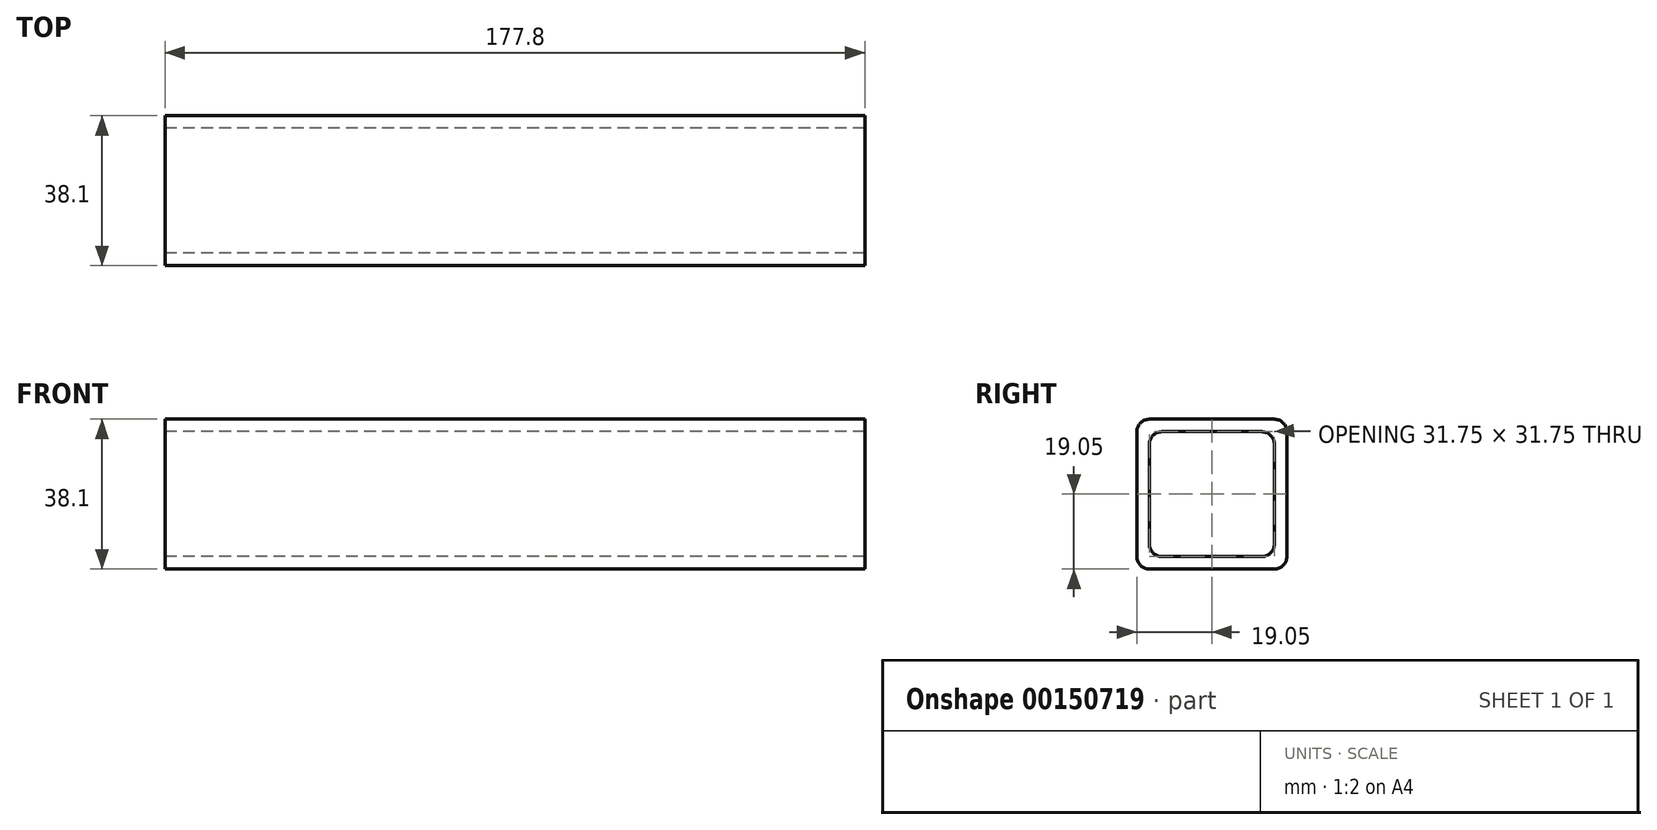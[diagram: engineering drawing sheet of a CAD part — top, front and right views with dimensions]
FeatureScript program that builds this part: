
annotation { "Feature Type Name" : "Feature", "Feature Type Description" : "" }
export const myFeature = defineFeature(function(context is Context, id is Id, definition is map)
    precondition{}
    {
        {
            var Q0;
            Q0=qCreatedBy(makeId("Right.planeOp"),FACE);
            var sketch = newSketch(context, id + "F0", { "sketchPlane" : qUnion([Q0])});
            skLineSegment(sketch, "E0.bottom", {"start": v(15.87, 19.05) * mm, "end": v(-15.88, 19.05) * mm});
            skLineSegment(sketch, "E0.top", {"start": v(15.88, -19.05) * mm, "end": v(-15.87, -19.05) * mm});
            skLineSegment(sketch, "E0.left", {"start": v(19.05, 15.88) * mm, "end": v(19.05, -15.88) * mm});
            skLineSegment(sketch, "E0.right", {"start": v(-19.05, 15.87) * mm, "end": v(-19.05, -15.88) * mm});
            skPoint(sketch, "E0.middle", {"position": v(0, 0) * mm});
            skPoint(sketch, "E1.visualSharp", {"position": v(-19.05, 19.05) * mm});
            skArc(sketch, "E1.filletArc", {"start": v(-15.88, 19.05) * mm, "mid": v(-18.12, 18.12) * mm, "end": v(-19.05, 15.87) * mm});
            skPoint(sketch, "E2.visualSharp", {"position": v(19.05, 19.05) * mm});
            skArc(sketch, "E2.filletArc", {"start": v(19.05, 15.88) * mm, "mid": v(18.12, 18.12) * mm, "end": v(15.87, 19.05) * mm});
            skPoint(sketch, "E3.visualSharp", {"position": v(-19.05, -19.05) * mm});
            skArc(sketch, "E3.filletArc", {"start": v(-19.05, -15.88) * mm, "mid": v(-18.12, -18.12) * mm, "end": v(-15.87, -19.05) * mm});
            skPoint(sketch, "E4.visualSharp", {"position": v(19.05, -19.05) * mm});
            skArc(sketch, "E4.filletArc", {"start": v(15.88, -19.05) * mm, "mid": v(18.12, -18.12) * mm, "end": v(19.05, -15.88) * mm});
            skLineSegment(sketch, "E5.bottom", {"start": v(12.7, 15.88) * mm, "end": v(-12.7, 15.88) * mm});
            skLineSegment(sketch, "E5.top", {"start": v(12.7, -15.88) * mm, "end": v(-12.7, -15.88) * mm});
            skLineSegment(sketch, "E5.left", {"start": v(15.87, 12.7) * mm, "end": v(15.88, -12.7) * mm});
            skLineSegment(sketch, "E5.right", {"start": v(-15.88, 12.7) * mm, "end": v(-15.87, -12.7) * mm});
            skArc(sketch, "E6.filletArc", {"start": v(-12.7, 15.88) * mm, "mid": v(-14.95, 14.95) * mm, "end": v(-15.88, 12.7) * mm});
            skArc(sketch, "E7.filletArc", {"start": v(15.88, 12.7) * mm, "mid": v(14.95, 14.95) * mm, "end": v(12.7, 15.88) * mm});
            skArc(sketch, "E8.filletArc", {"start": v(-15.88, -12.7) * mm, "mid": v(-14.95, -14.95) * mm, "end": v(-12.7, -15.88) * mm});
            skPoint(sketch, "E9.visualSharp", {"position": v(15.88, -15.87) * mm});
            skArc(sketch, "E9.filletArc", {"start": v(12.7, -15.88) * mm, "mid": v(14.95, -14.95) * mm, "end": v(15.88, -12.7) * mm});
            skSolve(sketch);
        }
        {
            var Q0;
            Q0 = qSketchRegion(id + "F0", true);
            extrude(context, id + "F1", {"entities" : qUnion([Q0]), "depth" : 177.8 * mm});
        }
    });
